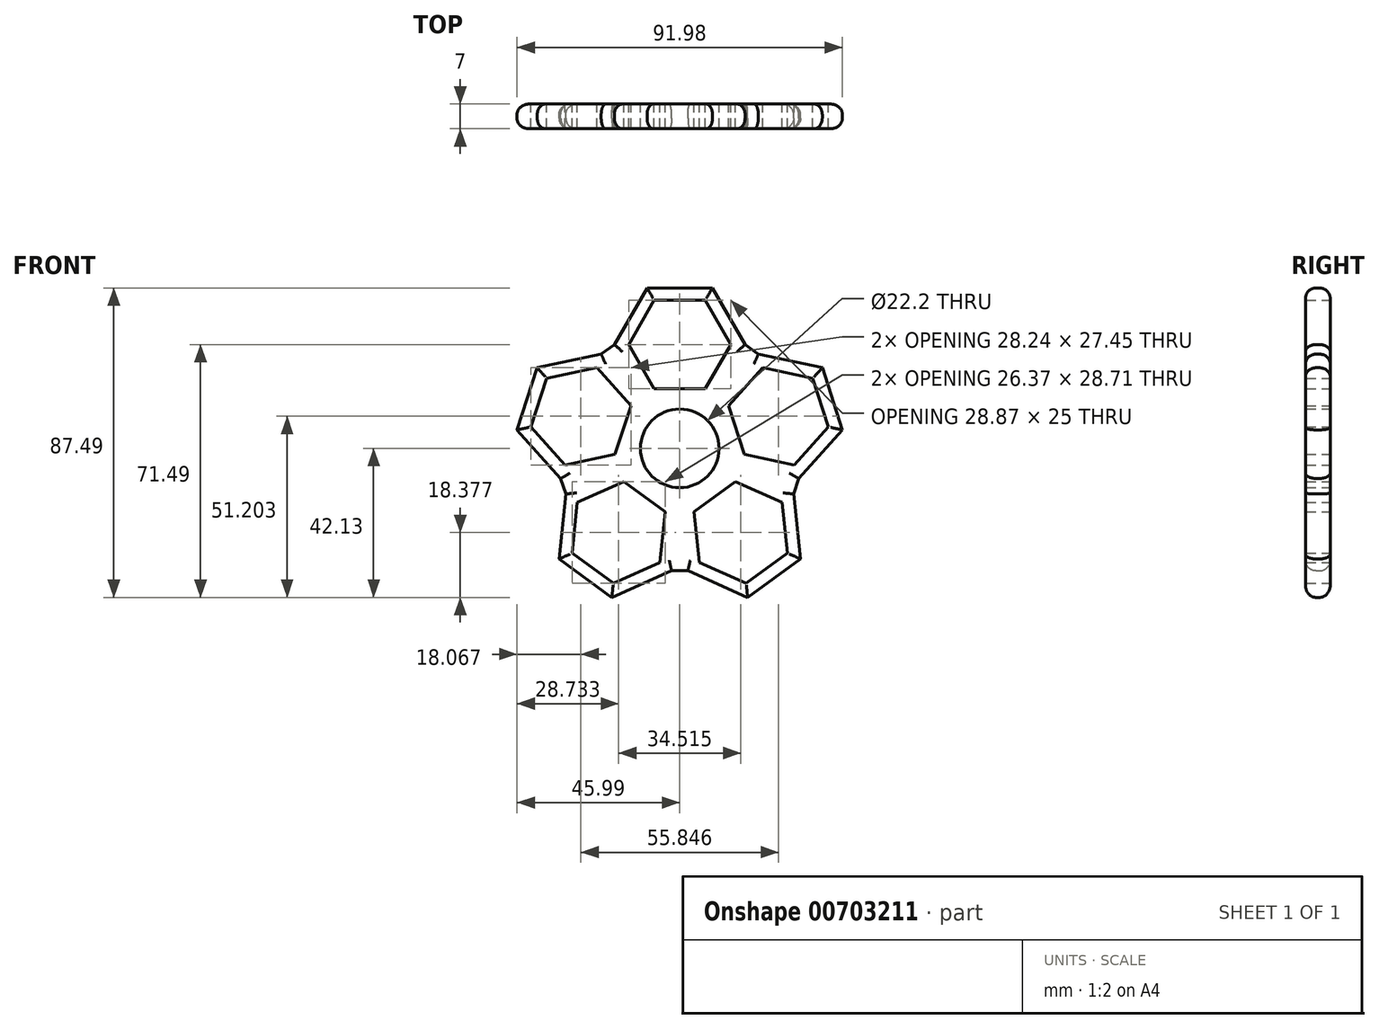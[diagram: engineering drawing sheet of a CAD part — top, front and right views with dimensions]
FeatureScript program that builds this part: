
annotation { "Feature Type Name" : "Feature", "Feature Type Description" : "" }
export const myFeature = defineFeature(function(context is Context, id is Id, definition is map)
    precondition{}
    {
        {
            var Q0;
            Q0=qCreatedBy(makeId("Front.planeOp"),FACE);
            var sketch = newSketch(context, id + "F0", { "sketchPlane" : qUnion([Q0])});
            skCircle(sketch, "E0", {"center": v(0, 0) * mm, "radius": 11.1 * mm});
            skCircle(sketch, "E1.cCircle", {"center": v(0, 29.36) * mm, "radius": 12.5 * mm, "construction": true});
            skLineSegment(sketch, "E1.0", {"start": v(7.22, 16.86) * mm, "end": v(-7.22, 16.86) * mm});
            skLineSegment(sketch, "E1.1", {"start": v(-7.22, 16.86) * mm, "end": v(-14.43, 29.36) * mm});
            skLineSegment(sketch, "E1.2", {"start": v(-14.43, 29.36) * mm, "end": v(-7.22, 41.86) * mm});
            skLineSegment(sketch, "E1.3", {"start": v(-7.22, 41.86) * mm, "end": v(7.22, 41.86) * mm});
            skLineSegment(sketch, "E1.4", {"start": v(7.22, 41.86) * mm, "end": v(14.43, 29.36) * mm});
            skLineSegment(sketch, "E1.5", {"start": v(14.43, 29.36) * mm, "end": v(7.22, 16.86) * mm});
            skPoint(sketch, "E1.0.midPoint", {"position": v(0, 16.86) * mm});
            skCircle(sketch, "E2.cCircle", {"center": v(0, 29.36) * mm, "radius": 16 * mm, "construction": true});
            skLineSegment(sketch, "E2.0", {"start": v(9.24, 13.36) * mm, "end": v(-9.24, 13.36) * mm});
            skLineSegment(sketch, "E2.1", {"start": v(-9.24, 13.36) * mm, "end": v(-18.48, 29.36) * mm});
            skLineSegment(sketch, "E2.2", {"start": v(-18.48, 29.36) * mm, "end": v(-9.24, 45.36) * mm});
            skLineSegment(sketch, "E2.3", {"start": v(-9.24, 45.36) * mm, "end": v(9.24, 45.36) * mm});
            skLineSegment(sketch, "E2.4", {"start": v(9.24, 45.36) * mm, "end": v(18.48, 29.36) * mm});
            skLineSegment(sketch, "E2.5", {"start": v(18.48, 29.36) * mm, "end": v(9.24, 13.36) * mm});
            skPoint(sketch, "E2.0.midPoint", {"position": v(0, 13.36) * mm});
            skPoint(sketch, "E3.1.0", {"position": v(-12.7, 4.13) * mm});
            skCircle(sketch, "E3.1.1", {"center": v(-27.92, 9.07) * mm, "radius": 12.5 * mm, "construction": true});
            skLineSegment(sketch, "E3.1.4", {"start": v(-32.38, -4.65) * mm, "end": v(-42.04, 6.07) * mm});
            skLineSegment(sketch, "E3.1.5", {"start": v(-22.21, 26.64) * mm, "end": v(-9.85, 12.91) * mm});
            skLineSegment(sketch, "E3.1.6", {"start": v(-40.29, 22.8) * mm, "end": v(-22.21, 26.64) * mm});
            skLineSegment(sketch, "E3.1.7", {"start": v(-46, 5.23) * mm, "end": v(-40.29, 22.8) * mm});
            skLineSegment(sketch, "E3.1.8", {"start": v(-18.27, -1.65) * mm, "end": v(-32.38, -4.65) * mm});
            skLineSegment(sketch, "E3.1.9", {"start": v(-42.04, 6.07) * mm, "end": v(-37.58, 19.8) * mm});
            skLineSegment(sketch, "E3.1.10", {"start": v(-37.58, 19.8) * mm, "end": v(-23.46, 22.8) * mm});
            skLineSegment(sketch, "E3.1.11", {"start": v(-23.46, 22.8) * mm, "end": v(-13.8, 12.07) * mm});
            skCircle(sketch, "E3.1.12", {"center": v(-27.92, 9.07) * mm, "radius": 16 * mm, "construction": true});
            skLineSegment(sketch, "E3.1.13", {"start": v(-9.85, 12.91) * mm, "end": v(-15.56, -4.66) * mm});
            skLineSegment(sketch, "E3.1.14", {"start": v(-15.56, -4.66) * mm, "end": v(-33.63, -8.5) * mm});
            skLineSegment(sketch, "E3.1.15", {"start": v(-33.63, -8.5) * mm, "end": v(-46, 5.23) * mm});
            skPoint(sketch, "E3.1.16", {"position": v(-16.03, 5.21) * mm});
            skLineSegment(sketch, "E3.1.17", {"start": v(-13.8, 12.07) * mm, "end": v(-18.27, -1.65) * mm});
            skPoint(sketch, "E3.2.0", {"position": v(-7.85, -10.8) * mm});
            skCircle(sketch, "E3.2.1", {"center": v(-17.26, -23.75) * mm, "radius": 12.5 * mm, "construction": true});
            skLineSegment(sketch, "E3.2.4", {"start": v(-5.58, -32.24) * mm, "end": v(-18.77, -38.1) * mm});
            skLineSegment(sketch, "E3.2.5", {"start": v(-32.2, -12.9) * mm, "end": v(-15.33, -5.38) * mm});
            skLineSegment(sketch, "E3.2.6", {"start": v(-34.14, -31.27) * mm, "end": v(-32.2, -12.9) * mm});
            skLineSegment(sketch, "E3.2.7", {"start": v(-19.19, -42.13) * mm, "end": v(-34.14, -31.27) * mm});
            skLineSegment(sketch, "E3.2.8", {"start": v(-4.07, -17.88) * mm, "end": v(-5.58, -32.24) * mm});
            skLineSegment(sketch, "E3.2.9", {"start": v(-18.77, -38.1) * mm, "end": v(-30.44, -29.62) * mm});
            skLineSegment(sketch, "E3.2.10", {"start": v(-30.44, -29.62) * mm, "end": v(-28.93, -15.27) * mm});
            skLineSegment(sketch, "E3.2.11", {"start": v(-28.93, -15.27) * mm, "end": v(-15.75, -9.4) * mm});
            skCircle(sketch, "E3.2.12", {"center": v(-17.26, -23.75) * mm, "radius": 16 * mm, "construction": true});
            skLineSegment(sketch, "E3.2.13", {"start": v(-15.33, -5.38) * mm, "end": v(-0.38, -16.24) * mm});
            skLineSegment(sketch, "E3.2.14", {"start": v(-0.38, -16.24) * mm, "end": v(-2.31, -34.61) * mm});
            skLineSegment(sketch, "E3.2.15", {"start": v(-2.31, -34.61) * mm, "end": v(-19.19, -42.13) * mm});
            skPoint(sketch, "E3.2.16", {"position": v(-9.91, -13.64) * mm});
            skLineSegment(sketch, "E3.2.17", {"start": v(-15.75, -9.4) * mm, "end": v(-4.07, -17.88) * mm});
            skPoint(sketch, "E3.3.0", {"position": v(7.85, -10.8) * mm});
            skCircle(sketch, "E3.3.1", {"center": v(17.26, -23.75) * mm, "radius": 12.5 * mm, "construction": true});
            skCircle(sketch, "E3.3.3", {"center": v(0, 0) * mm, "radius": 12.25 * mm});
            skLineSegment(sketch, "E3.3.4", {"start": v(28.93, -15.27) * mm, "end": v(30.44, -29.62) * mm});
            skLineSegment(sketch, "E3.3.5", {"start": v(2.31, -34.61) * mm, "end": v(0.38, -16.24) * mm});
            skLineSegment(sketch, "E3.3.6", {"start": v(19.19, -42.13) * mm, "end": v(2.31, -34.61) * mm});
            skLineSegment(sketch, "E3.3.7", {"start": v(34.14, -31.27) * mm, "end": v(19.19, -42.13) * mm});
            skLineSegment(sketch, "E3.3.8", {"start": v(15.75, -9.4) * mm, "end": v(28.93, -15.27) * mm});
            skLineSegment(sketch, "E3.3.9", {"start": v(30.44, -29.62) * mm, "end": v(18.77, -38.1) * mm});
            skLineSegment(sketch, "E3.3.10", {"start": v(18.77, -38.1) * mm, "end": v(5.58, -32.24) * mm});
            skLineSegment(sketch, "E3.3.11", {"start": v(5.58, -32.24) * mm, "end": v(4.07, -17.88) * mm});
            skCircle(sketch, "E3.3.12", {"center": v(17.26, -23.75) * mm, "radius": 16 * mm, "construction": true});
            skLineSegment(sketch, "E3.3.13", {"start": v(0.38, -16.24) * mm, "end": v(15.33, -5.38) * mm});
            skLineSegment(sketch, "E3.3.14", {"start": v(15.33, -5.38) * mm, "end": v(32.2, -12.9) * mm});
            skLineSegment(sketch, "E3.3.15", {"start": v(32.2, -12.9) * mm, "end": v(34.14, -31.27) * mm});
            skPoint(sketch, "E3.3.16", {"position": v(9.91, -13.64) * mm});
            skLineSegment(sketch, "E3.3.17", {"start": v(4.07, -17.88) * mm, "end": v(15.75, -9.4) * mm});
            skPoint(sketch, "E3.4.0", {"position": v(12.7, 4.13) * mm});
            skCircle(sketch, "E3.4.1", {"center": v(27.92, 9.07) * mm, "radius": 12.5 * mm, "construction": true});
            skCircle(sketch, "E3.4.3", {"center": v(0, 0) * mm, "radius": 12.25 * mm});
            skLineSegment(sketch, "E3.4.4", {"start": v(23.46, 22.8) * mm, "end": v(37.58, 19.8) * mm});
            skLineSegment(sketch, "E3.4.5", {"start": v(33.63, -8.5) * mm, "end": v(15.56, -4.66) * mm});
            skLineSegment(sketch, "E3.4.6", {"start": v(46, 5.23) * mm, "end": v(33.63, -8.5) * mm});
            skLineSegment(sketch, "E3.4.7", {"start": v(40.29, 22.8) * mm, "end": v(46, 5.23) * mm});
            skLineSegment(sketch, "E3.4.8", {"start": v(13.8, 12.07) * mm, "end": v(23.46, 22.8) * mm});
            skLineSegment(sketch, "E3.4.9", {"start": v(37.58, 19.8) * mm, "end": v(42.04, 6.07) * mm});
            skLineSegment(sketch, "E3.4.10", {"start": v(42.04, 6.07) * mm, "end": v(32.38, -4.65) * mm});
            skLineSegment(sketch, "E3.4.11", {"start": v(32.38, -4.65) * mm, "end": v(18.27, -1.65) * mm});
            skCircle(sketch, "E3.4.12", {"center": v(27.92, 9.07) * mm, "radius": 16 * mm, "construction": true});
            skLineSegment(sketch, "E3.4.13", {"start": v(15.56, -4.66) * mm, "end": v(9.85, 12.91) * mm});
            skLineSegment(sketch, "E3.4.14", {"start": v(9.85, 12.91) * mm, "end": v(22.21, 26.64) * mm});
            skLineSegment(sketch, "E3.4.15", {"start": v(22.21, 26.64) * mm, "end": v(40.29, 22.8) * mm});
            skPoint(sketch, "E3.4.16", {"position": v(16.03, 5.21) * mm});
            skLineSegment(sketch, "E3.4.17", {"start": v(18.27, -1.65) * mm, "end": v(13.8, 12.07) * mm});
            skLineSegment(sketch, "E4", {"start": v(18.48, 29.36) * mm, "end": v(22.21, 26.64) * mm});
            skLineSegment(sketch, "E5.1.0", {"start": v(-22.21, 26.64) * mm, "end": v(-18.48, 29.36) * mm});
            skLineSegment(sketch, "E5.2.0", {"start": v(-32.2, -12.9) * mm, "end": v(-33.63, -8.5) * mm});
            skLineSegment(sketch, "E5.3.0", {"start": v(2.31, -34.61) * mm, "end": v(-2.31, -34.61) * mm});
            skLineSegment(sketch, "E5.4.0", {"start": v(33.63, -8.5) * mm, "end": v(32.2, -12.9) * mm});
            skSolve(sketch);
        }
        {
            var Q0;
            Q0 = qSketchRegion(id + "F0", true);
            var Q1;
            Q1=makeQuery(id+"F0.imprint","IMPRINT",FACE,{"disambiguationData":[TD([[makeQuery(id+"F0.imprint","IMPRINT",EDGE,{"derivedFrom":sQuery(id+"F0.wireOp",EDGE,"E0")}),-1.0]])]});
            extrude(context, id + "F1", {"entities" : qUnion([Q0, Q1]), "depth" : 7 * mm, "offsetDistance" : 25 * mm});
        }
        {
            var Q0;
            Q0=makeQuery(id+"F1.opExtrude","CAP_EDGE",EDGE,{"disambiguationData":[OSD([sQuery(id+"F0.wireOp",EDGE,"E2.3")])],"isStart":false});
            var Q1;
            Q1=makeQuery(id+"F1.opExtrude","CAP_EDGE",EDGE,{"disambiguationData":[OSD([sQuery(id+"F0.wireOp",EDGE,"E2.4")])],"isStart":false});
            var Q2;
            Q2=makeQuery(id+"F1.opExtrude","CAP_EDGE",EDGE,{"disambiguationData":[OSD([sQuery(id+"F0.wireOp",EDGE,"E3.4.15")])],"isStart":false});
            var Q3;
            Q3=makeQuery(id+"F1.opExtrude","CAP_EDGE",EDGE,{"disambiguationData":[OSD([sQuery(id+"F0.wireOp",EDGE,"E4")])],"isStart":false});
            var Q4;
            Q4=makeQuery(id+"F1.opExtrude","CAP_EDGE",EDGE,{"disambiguationData":[OSD([sQuery(id+"F0.wireOp",EDGE,"E3.4.7")])],"isStart":false});
            var Q5;
            Q5=makeQuery(id+"F1.opExtrude","CAP_EDGE",EDGE,{"disambiguationData":[OSD([sQuery(id+"F0.wireOp",EDGE,"E3.4.6")])],"isStart":false});
            var Q6;
            Q6=makeQuery(id+"F1.opExtrude","CAP_EDGE",EDGE,{"disambiguationData":[OSD([sQuery(id+"F0.wireOp",EDGE,"E3.3.15")])],"isStart":false});
            var Q7;
            Q7=makeQuery(id+"F1.opExtrude","CAP_EDGE",EDGE,{"disambiguationData":[OSD([sQuery(id+"F0.wireOp",EDGE,"E5.4.0")])],"isStart":false});
            var Q8;
            Q8=makeQuery(id+"F1.opExtrude","CAP_EDGE",EDGE,{"disambiguationData":[OSD([sQuery(id+"F0.wireOp",EDGE,"E3.3.7")])],"isStart":false});
            var Q9;
            Q9=makeQuery(id+"F1.opExtrude","CAP_EDGE",EDGE,{"disambiguationData":[OSD([sQuery(id+"F0.wireOp",EDGE,"E3.3.6")])],"isStart":false});
            var Q10;
            Q10=makeQuery(id+"F1.opExtrude","CAP_EDGE",EDGE,{"disambiguationData":[OSD([sQuery(id+"F0.wireOp",EDGE,"E3.2.15")])],"isStart":false});
            var Q11;
            Q11=makeQuery(id+"F1.opExtrude","CAP_EDGE",EDGE,{"disambiguationData":[OSD([sQuery(id+"F0.wireOp",EDGE,"E5.3.0")])],"isStart":false});
            var Q12;
            Q12=makeQuery(id+"F1.opExtrude","CAP_EDGE",EDGE,{"disambiguationData":[OSD([sQuery(id+"F0.wireOp",EDGE,"E3.2.7")])],"isStart":false});
            var Q13;
            Q13=makeQuery(id+"F1.opExtrude","CAP_EDGE",EDGE,{"disambiguationData":[OSD([sQuery(id+"F0.wireOp",EDGE,"E3.2.6")])],"isStart":false});
            var Q14;
            Q14=makeQuery(id+"F1.opExtrude","CAP_EDGE",EDGE,{"disambiguationData":[OSD([sQuery(id+"F0.wireOp",EDGE,"E5.2.0")])],"isStart":false});
            var Q15;
            Q15=makeQuery(id+"F1.opExtrude","CAP_EDGE",EDGE,{"disambiguationData":[OSD([sQuery(id+"F0.wireOp",EDGE,"E3.1.7")])],"isStart":false});
            var Q16;
            Q16=makeQuery(id+"F1.opExtrude","CAP_EDGE",EDGE,{"disambiguationData":[OSD([sQuery(id+"F0.wireOp",EDGE,"E3.1.15")])],"isStart":false});
            var Q17;
            Q17=makeQuery(id+"F1.opExtrude","CAP_EDGE",EDGE,{"disambiguationData":[OSD([sQuery(id+"F0.wireOp",EDGE,"E3.1.6")])],"isStart":false});
            var Q18;
            Q18=makeQuery(id+"F1.opExtrude","CAP_EDGE",EDGE,{"disambiguationData":[OSD([sQuery(id+"F0.wireOp",EDGE,"E5.1.0")])],"isStart":false});
            var Q19;
            Q19=makeQuery(id+"F1.opExtrude","CAP_EDGE",EDGE,{"disambiguationData":[OSD([sQuery(id+"F0.wireOp",EDGE,"E2.2")])],"isStart":false});
            var Q20;
            Q20=makeQuery(id+"F1.opExtrude","CAP_EDGE",EDGE,{"disambiguationData":[OSD([sQuery(id+"F0.wireOp",EDGE,"E3.2.7")])],"isStart":true});
            var Q21;
            Q21=makeQuery(id+"F1.opExtrude","CAP_EDGE",EDGE,{"disambiguationData":[OSD([sQuery(id+"F0.wireOp",EDGE,"E3.2.15")])],"isStart":true});
            var Q22;
            Q22=makeQuery(id+"F1.opExtrude","CAP_EDGE",EDGE,{"disambiguationData":[OSD([sQuery(id+"F0.wireOp",EDGE,"E5.3.0")])],"isStart":true});
            var Q23;
            Q23=makeQuery(id+"F1.opExtrude","CAP_EDGE",EDGE,{"disambiguationData":[OSD([sQuery(id+"F0.wireOp",EDGE,"E3.3.6")])],"isStart":true});
            var Q24;
            Q24=makeQuery(id+"F1.opExtrude","CAP_EDGE",EDGE,{"disambiguationData":[OSD([sQuery(id+"F0.wireOp",EDGE,"E3.3.7")])],"isStart":true});
            var Q25;
            Q25=makeQuery(id+"F1.opExtrude","CAP_EDGE",EDGE,{"disambiguationData":[OSD([sQuery(id+"F0.wireOp",EDGE,"E3.3.15")])],"isStart":true});
            var Q26;
            Q26=makeQuery(id+"F1.opExtrude","CAP_EDGE",EDGE,{"disambiguationData":[OSD([sQuery(id+"F0.wireOp",EDGE,"E3.4.6")])],"isStart":true});
            var Q27;
            Q27=makeQuery(id+"F1.opExtrude","CAP_EDGE",EDGE,{"disambiguationData":[OSD([sQuery(id+"F0.wireOp",EDGE,"E3.4.7")])],"isStart":true});
            var Q28;
            Q28=makeQuery(id+"F1.opExtrude","CAP_EDGE",EDGE,{"disambiguationData":[OSD([sQuery(id+"F0.wireOp",EDGE,"E3.4.15")])],"isStart":true});
            var Q29;
            Q29=makeQuery(id+"F1.opExtrude","CAP_EDGE",EDGE,{"disambiguationData":[OSD([sQuery(id+"F0.wireOp",EDGE,"E5.4.0")])],"isStart":true});
            var Q30;
            Q30=makeQuery(id+"F1.opExtrude","CAP_EDGE",EDGE,{"disambiguationData":[OSD([sQuery(id+"F0.wireOp",EDGE,"E4")])],"isStart":true});
            var Q31;
            Q31=makeQuery(id+"F1.opExtrude","CAP_EDGE",EDGE,{"disambiguationData":[OSD([sQuery(id+"F0.wireOp",EDGE,"E2.4")])],"isStart":true});
            var Q32;
            Q32=makeQuery(id+"F1.opExtrude","CAP_EDGE",EDGE,{"disambiguationData":[OSD([sQuery(id+"F0.wireOp",EDGE,"E2.3")])],"isStart":true});
            var Q33;
            Q33=makeQuery(id+"F1.opExtrude","CAP_EDGE",EDGE,{"disambiguationData":[OSD([sQuery(id+"F0.wireOp",EDGE,"E2.2")])],"isStart":true});
            var Q34;
            Q34=makeQuery(id+"F1.opExtrude","CAP_EDGE",EDGE,{"disambiguationData":[OSD([sQuery(id+"F0.wireOp",EDGE,"E5.1.0")])],"isStart":true});
            var Q35;
            Q35=makeQuery(id+"F1.opExtrude","CAP_EDGE",EDGE,{"disambiguationData":[OSD([sQuery(id+"F0.wireOp",EDGE,"E3.1.6")])],"isStart":true});
            var Q36;
            Q36=makeQuery(id+"F1.opExtrude","CAP_EDGE",EDGE,{"disambiguationData":[OSD([sQuery(id+"F0.wireOp",EDGE,"E3.1.7")])],"isStart":true});
            var Q37;
            Q37=makeQuery(id+"F1.opExtrude","CAP_EDGE",EDGE,{"disambiguationData":[OSD([sQuery(id+"F0.wireOp",EDGE,"E3.2.6")])],"isStart":true});
            var Q38;
            Q38=makeQuery(id+"F1.opExtrude","CAP_EDGE",EDGE,{"disambiguationData":[OSD([sQuery(id+"F0.wireOp",EDGE,"E3.1.15")])],"isStart":true});
            var Q39;
            Q39=makeQuery(id+"F1.opExtrude","CAP_EDGE",EDGE,{"disambiguationData":[OSD([sQuery(id+"F0.wireOp",EDGE,"E5.2.0")])],"isStart":true});
            fillet(context, id + "F2", {"entities" : qUnion([Q0, Q1, Q2, Q3, Q4, Q5, Q6, Q7, Q8, Q9, Q10, Q11, Q12, Q13, Q14, Q15, Q16, Q17, Q18, Q19, Q20, Q21, Q22, Q23, Q24, Q25, Q26, Q27, Q28, Q29, Q30, Q31, Q32, Q33, Q34, Q35, Q36, Q37, Q38, Q39]), "radius" : 3 * mm, "tangentPropagation" : true, "allowEdgeOverflow" : false});
        }
    });
